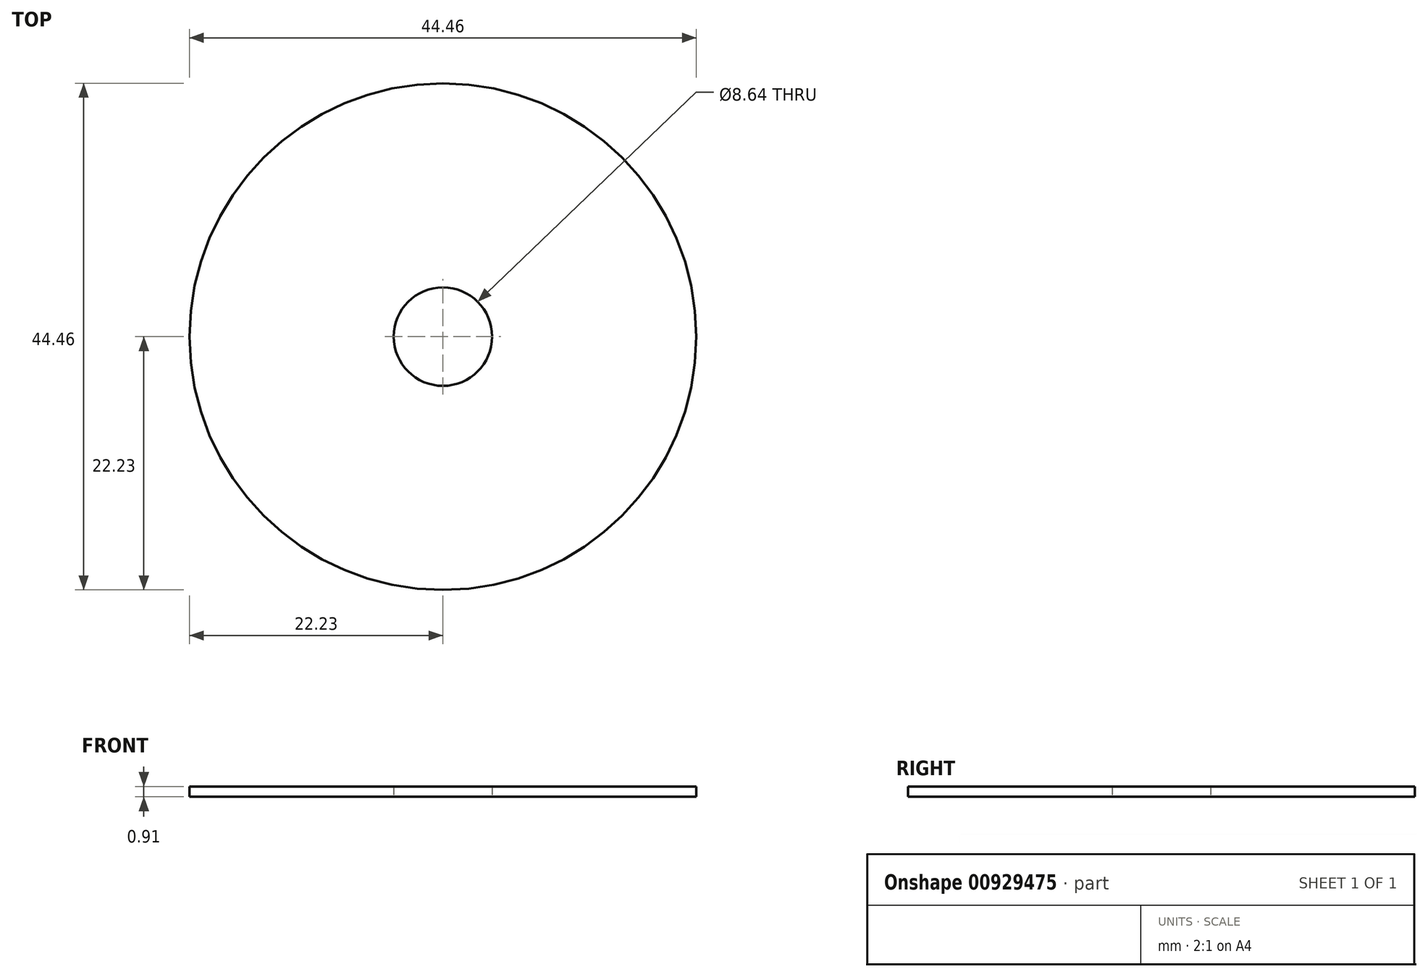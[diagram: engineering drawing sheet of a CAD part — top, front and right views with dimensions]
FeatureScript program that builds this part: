
annotation { "Feature Type Name" : "Feature", "Feature Type Description" : "" }
export const myFeature = defineFeature(function(context is Context, id is Id, definition is map)
    precondition{}
    {
        {
            var Q0;
            Q0=qCreatedBy(makeId("Top.planeOp"),FACE);
            var sketch = newSketch(context, id + "F0", { "sketchPlane" : qUnion([Q0])});
            skCircle(sketch, "E0", {"center": v(0, 0) * mm, "radius": 22.23 * mm});
            skCircle(sketch, "E1", {"center": v(0, 0) * mm, "radius": 4.32 * mm});
            skSolve(sketch);
        }
        {
            var Q0;
            Q0=makeQuery(id+"F0.imprint","IMPRINT",FACE,{"disambiguationData":[TD([[makeQuery(id+"F0.imprint","IMPRINT",EDGE,{"derivedFrom":sQuery(id+"F0.wireOp",EDGE,"E0")}),1.0]])]});
            extrude(context, id + "F1", {"entities" : qUnion([Q0]), "depth" : 0.91 * mm, "offsetDistance" : 25.4 * mm});
        }
    });
